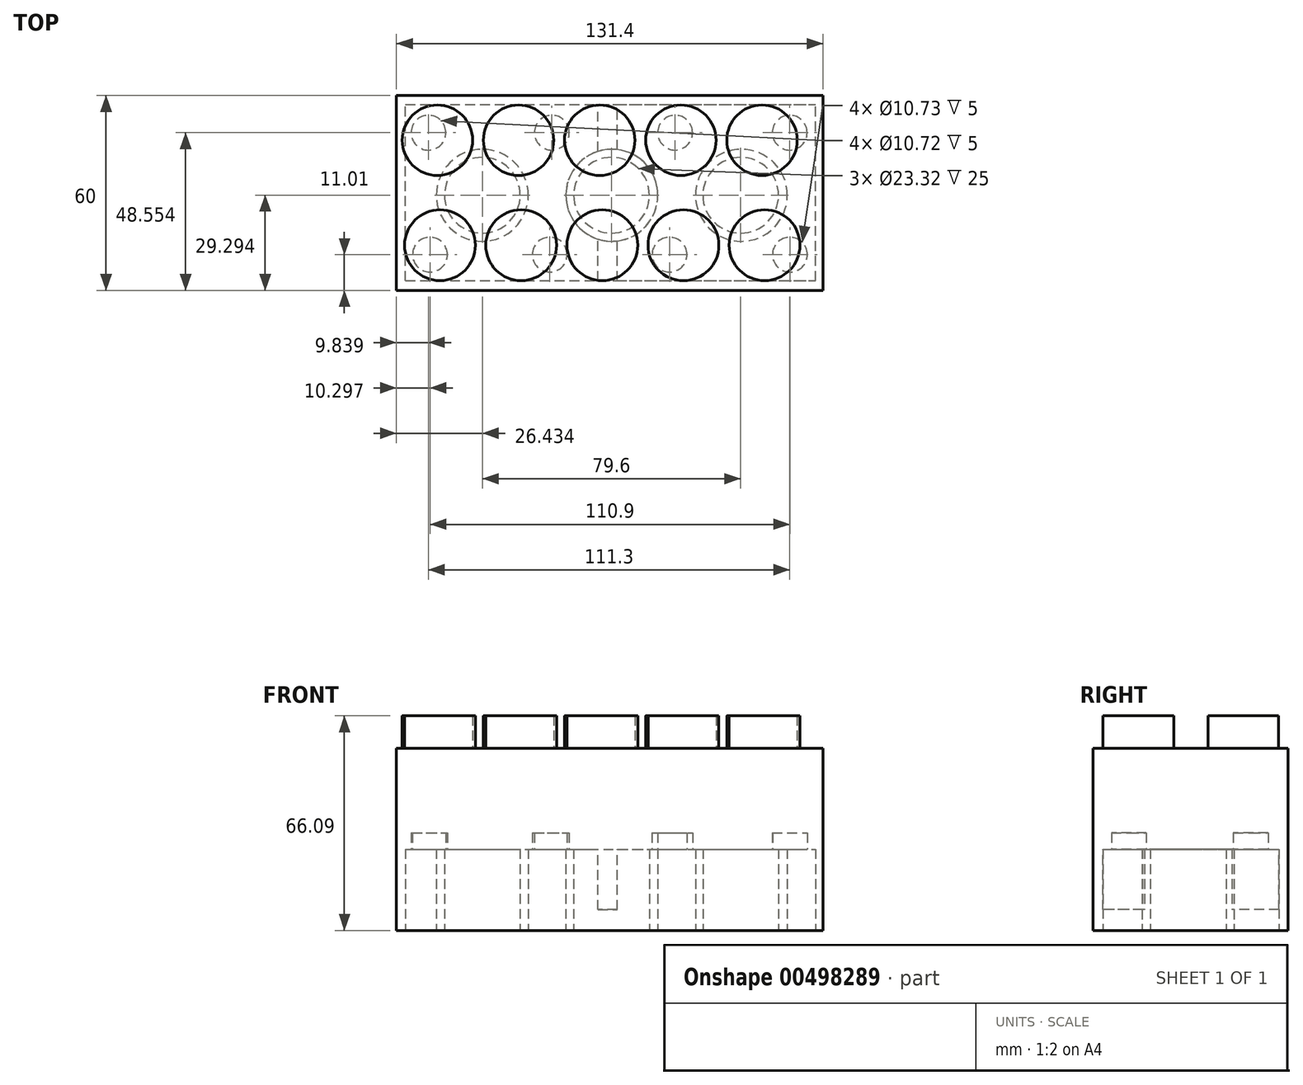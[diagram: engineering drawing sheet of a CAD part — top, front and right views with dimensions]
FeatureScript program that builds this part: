
annotation { "Feature Type Name" : "Feature", "Feature Type Description" : "" }
export const myFeature = defineFeature(function(context is Context, id is Id, definition is map)
    precondition{}
    {
        {
            var Q0;
            Q0=qCreatedBy(makeId("Front.planeOp"),FACE);
            var sketch = newSketch(context, id + "F0", { "sketchPlane" : qUnion([Q0])});
            skLineSegment(sketch, "E0.bottom", {"start": v(-65.01, 21.75) * mm, "end": v(66.39, 21.75) * mm});
            skLineSegment(sketch, "E0.top", {"start": v(-65.01, -34.34) * mm, "end": v(66.39, -34.34) * mm});
            skLineSegment(sketch, "E0.left", {"start": v(-65.01, 21.75) * mm, "end": v(-65.01, -34.34) * mm});
            skLineSegment(sketch, "E0.right", {"start": v(66.39, 21.75) * mm, "end": v(66.39, -34.34) * mm});
            skSolve(sketch);
        }
        {
            var Q0;
            Q0=makeQuery(id+"F0.imprint","IMPRINT",FACE,{"disambiguationData":[TD([[makeQuery(id+"F0.imprint","IMPRINT",EDGE,{"derivedFrom":sQuery(id+"F0.wireOp",EDGE,"E0.bottom")}),-1.0]])]});
            extrude(context, id + "F1", {"entities" : qUnion([Q0]), "depth" : 60 * mm});
        }
        {
            var Q0;
            Q0=makeQuery(id+"F1.opExtrude","SWEPT_FACE",FACE,{"disambiguationData":[OSD([sQuery(id+"F0.wireOp",EDGE,"E0.bottom")])]});
            var sketch = newSketch(context, id + "F2", { "sketchPlane" : qUnion([Q0])});
            skCircle(sketch, "E1", {"center": v(-51.62, -46.09) * mm, "radius": 10.9 * mm});
            skCircle(sketch, "E2.1.0.0", {"center": v(-26.62, -46.09) * mm, "radius": 10.9 * mm});
            skCircle(sketch, "E2.2.0.0", {"center": v(-1.62, -46.09) * mm, "radius": 10.9 * mm});
            skLineSegment(sketch, "E2.direction1", {"start": v(-51.62, -46.09) * mm, "end": v(-26.62, -46.09) * mm, "construction": true});
            skCircle(sketch, "E3.1.0.0", {"center": v(23.38, -46.09) * mm, "radius": 10.9 * mm});
            skCircle(sketch, "E3.2.0.0", {"center": v(48.38, -46.09) * mm, "radius": 10.9 * mm});
            skLineSegment(sketch, "E3.direction1", {"start": v(-1.62, -46.09) * mm, "end": v(23.38, -46.09) * mm, "construction": true});
            skSolve(sketch);
        }
        {
            var Q0;
            Q0 = qSketchRegion(id + "F2", true);
            extrude(context, id + "F3", {"entities" : qUnion([Q0]), "operationType" : NewBodyOperationType.ADD, "depth" : 10 * mm});
        }
        {
            var Q0;
            Q0=makeQuery(id+"F1.opExtrude","SWEPT_FACE",FACE,{"disambiguationData":[OSD([sQuery(id+"F0.wireOp",EDGE,"E0.bottom")])]});
            var sketch = newSketch(context, id + "F4", { "sketchPlane" : qUnion([Q0])});
            skCircle(sketch, "E4", {"center": v(-52.41, -13.75) * mm, "radius": 10.84 * mm});
            skCircle(sketch, "E5.1.0.0", {"center": v(-27.41, -13.75) * mm, "radius": 10.84 * mm});
            skCircle(sketch, "E5.2.0.0", {"center": v(-2.41, -13.75) * mm, "radius": 10.84 * mm});
            skLineSegment(sketch, "E5.direction1", {"start": v(-52.41, -13.75) * mm, "end": v(-27.41, -13.75) * mm, "construction": true});
            skCircle(sketch, "E6.1.0.0", {"center": v(22.59, -13.75) * mm, "radius": 10.84 * mm});
            skCircle(sketch, "E6.2.0.0", {"center": v(47.59, -13.75) * mm, "radius": 10.84 * mm});
            skLineSegment(sketch, "E6.direction1", {"start": v(-2.41, -13.75) * mm, "end": v(22.59, -13.75) * mm, "construction": true});
            skSolve(sketch);
        }
        {
            var Q0;
            Q0=makeQuery(id+"F4.imprint","IMPRINT",FACE,{"disambiguationData":[TD([[makeQuery(id+"F4.imprint","IMPRINT",EDGE,{"derivedFrom":sQuery(id+"F4.wireOp",EDGE,"E4")}),1.0]])]});
            var Q1;
            Q1=makeQuery(id+"F4.imprint","IMPRINT",FACE,{"disambiguationData":[TD([[makeQuery(id+"F4.imprint","IMPRINT",EDGE,{"derivedFrom":sQuery(id+"F4.wireOp",EDGE,"E5.1.0.0")}),1.0]])]});
            var Q2;
            Q2=makeQuery(id+"F4.imprint","IMPRINT",FACE,{"disambiguationData":[TD([[makeQuery(id+"F4.imprint","IMPRINT",EDGE,{"derivedFrom":sQuery(id+"F4.wireOp",EDGE,"E5.2.0.0")}),1.0]])]});
            var Q3;
            Q3=makeQuery(id+"F4.imprint","IMPRINT",FACE,{"disambiguationData":[TD([[makeQuery(id+"F4.imprint","IMPRINT",EDGE,{"derivedFrom":sQuery(id+"F4.wireOp",EDGE,"E6.1.0.0")}),1.0]])]});
            var Q4;
            Q4=makeQuery(id+"F4.imprint","IMPRINT",FACE,{"disambiguationData":[TD([[makeQuery(id+"F4.imprint","IMPRINT",EDGE,{"derivedFrom":sQuery(id+"F4.wireOp",EDGE,"E6.2.0.0")}),1.0]])]});
            extrude(context, id + "F5", {"entities" : qUnion([Q0, Q1, Q2, Q3, Q4]), "operationType" : NewBodyOperationType.ADD, "depth" : 10 * mm});
        }
        {
            var Q0;
            Q0=makeQuery(id+"F1.opExtrude","SWEPT_FACE",FACE,{"disambiguationData":[OSD([sQuery(id+"F0.wireOp",EDGE,"E0.top")])]});
            var sketch = newSketch(context, id + "F6", { "sketchPlane" : qUnion([Q0])});
            skCircle(sketch, "E7", {"center": v(41.22, 30.7) * mm, "radius": 14.16 * mm});
            skCircle(sketch, "E8.1.0.0", {"center": v(1.32, 30.7) * mm, "radius": 14.16 * mm});
            skCircle(sketch, "E8.2.0.0", {"center": v(-38.58, 30.7) * mm, "radius": 14.16 * mm});
            skLineSegment(sketch, "E8.direction1", {"start": v(41.22, 30.7) * mm, "end": v(1.32, 30.7) * mm, "construction": true});
            skLineSegment(sketch, "E9.bottom", {"start": v(-62.27, 57) * mm, "end": v(64.1, 57) * mm});
            skLineSegment(sketch, "E9.top", {"start": v(-62.27, 2.75) * mm, "end": v(64.1, 2.75) * mm});
            skLineSegment(sketch, "E9.left", {"start": v(-62.27, 57) * mm, "end": v(-62.27, 2.75) * mm});
            skLineSegment(sketch, "E9.right", {"start": v(64.1, 57) * mm, "end": v(64.1, 2.75) * mm});
            skCircle(sketch, "E10", {"center": v(-38.58, 30.7) * mm, "radius": 11.66 * mm});
            skCircle(sketch, "E11.1.0.0", {"center": v(1.22, 30.7) * mm, "radius": 11.66 * mm});
            skCircle(sketch, "E11.2.0.0", {"center": v(41.02, 30.7) * mm, "radius": 11.66 * mm});
            skLineSegment(sketch, "E11.direction1", {"start": v(-38.58, 30.7) * mm, "end": v(1.22, 30.7) * mm, "construction": true});
            skCircle(sketch, "E12", {"center": v(-54.71, 48.99) * mm, "radius": 5.36 * mm});
            skCircle(sketch, "E13.1.0.0", {"center": v(-17.81, 48.99) * mm, "radius": 5.36 * mm});
            skCircle(sketch, "E13.2.0.0", {"center": v(19.09, 48.99) * mm, "radius": 5.36 * mm});
            skLineSegment(sketch, "E13.direction1", {"start": v(-54.71, 48.99) * mm, "end": v(-17.81, 48.99) * mm, "construction": true});
            skCircle(sketch, "E14.1.0.0", {"center": v(56.19, 48.99) * mm, "radius": 5.36 * mm});
            skCircle(sketch, "E14.2.0.0", {"center": v(93.29, 48.99) * mm, "radius": 5.36 * mm});
            skLineSegment(sketch, "E14.direction1", {"start": v(19.09, 48.99) * mm, "end": v(56.19, 48.99) * mm, "construction": true});
            skCircle(sketch, "E15", {"center": v(-55.17, 11.45) * mm, "radius": 5.36 * mm});
            skCircle(sketch, "E16.1.0.0", {"center": v(-17.17, 11.45) * mm, "radius": 5.36 * mm});
            skCircle(sketch, "E16.2.0.0", {"center": v(20.83, 11.45) * mm, "radius": 5.36 * mm});
            skLineSegment(sketch, "E16.direction1", {"start": v(-55.17, 11.45) * mm, "end": v(-17.17, 11.45) * mm, "construction": true});
            skCircle(sketch, "E17.1.0.0", {"center": v(56.13, 11.45) * mm, "radius": 5.36 * mm});
            skCircle(sketch, "E17.2.0.0", {"center": v(91.43, 11.45) * mm, "radius": 5.36 * mm});
            skLineSegment(sketch, "E17.direction1", {"start": v(20.83, 11.45) * mm, "end": v(56.13, 11.45) * mm, "construction": true});
            skSolve(sketch);
        }
        {
            var Q0;
            Q0=makeQuery(id+"F6.imprint","IMPRINT",FACE,{"disambiguationData":[TD([[makeQuery(id+"F6.imprint","IMPRINT",EDGE,{"derivedFrom":sQuery(id+"F6.wireOp",EDGE,"E7")}),-1.0]])]});
            var Q1;
            Q1=makeQuery(id+"F6.imprint","IMPRINT",FACE,{"disambiguationData":[TD([[makeQuery(id+"F6.imprint","IMPRINT",EDGE,{"derivedFrom":sQuery(id+"F6.wireOp",EDGE,"E10")}),1.0]])]});
            var Q2;
            Q2=makeQuery(id+"F6.imprint","IMPRINT",FACE,{"disambiguationData":[TD([[makeQuery(id+"F6.imprint","IMPRINT",EDGE,{"derivedFrom":sQuery(id+"F6.wireOp",EDGE,"E11.1.0.0")}),1.0]])]});
            var Q3;
            Q3=makeQuery(id+"F6.imprint","IMPRINT",FACE,{"disambiguationData":[TD([[makeQuery(id+"F6.imprint","IMPRINT",EDGE,{"derivedFrom":sQuery(id+"F6.wireOp",EDGE,"E11.2.0.0")}),1.0]])]});
            extrude(context, id + "F7", {"entities" : qUnion([Q0, Q1, Q2, Q3]), "operationType" : NewBodyOperationType.REMOVE, "oppositeDirection" : true, "depth" : 25 * mm});
        }
        {
            var Q0;
            Q0=makeQuery(id+"F7.boolean.opBoolean","SPLIT",FACE,{"disambiguationData":[TD([makeQuery(id+"F7.opExtrude","SWEPT_FACE",FACE,{"disambiguationData":[OSD([sQuery(id+"F6.wireOp",EDGE,"E12")])]})])],"derivedFrom":makeQuery(id+"F1.opExtrude","SWEPT_FACE",FACE,{"disambiguationData":[OSD([sQuery(id+"F0.wireOp",EDGE,"E0.top")])]})});
            var Q1;
            Q1=makeQuery(id+"F7.boolean.opBoolean","SPLIT",FACE,{"disambiguationData":[TD([makeQuery(id+"F7.opExtrude","SWEPT_FACE",FACE,{"disambiguationData":[OSD([sQuery(id+"F6.wireOp",EDGE,"E13.1.0.0")])]})])],"derivedFrom":makeQuery(id+"F1.opExtrude","SWEPT_FACE",FACE,{"disambiguationData":[OSD([sQuery(id+"F0.wireOp",EDGE,"E0.top")])]})});
            var Q2;
            Q2=makeQuery(id+"F7.boolean.opBoolean","SPLIT",FACE,{"disambiguationData":[TD([makeQuery(id+"F7.opExtrude","SWEPT_FACE",FACE,{"disambiguationData":[OSD([sQuery(id+"F6.wireOp",EDGE,"E13.2.0.0")])]})])],"derivedFrom":makeQuery(id+"F1.opExtrude","SWEPT_FACE",FACE,{"disambiguationData":[OSD([sQuery(id+"F0.wireOp",EDGE,"E0.top")])]})});
            var Q3;
            Q3=makeQuery(id+"F7.boolean.opBoolean","SPLIT",FACE,{"disambiguationData":[TD([makeQuery(id+"F7.opExtrude","SWEPT_FACE",FACE,{"disambiguationData":[OSD([sQuery(id+"F6.wireOp",EDGE,"E14.1.0.0")])]})])],"derivedFrom":makeQuery(id+"F1.opExtrude","SWEPT_FACE",FACE,{"disambiguationData":[OSD([sQuery(id+"F0.wireOp",EDGE,"E0.top")])]})});
            var Q4;
            Q4=makeQuery(id+"F7.boolean.opBoolean","SPLIT",FACE,{"disambiguationData":[TD([makeQuery(id+"F7.opExtrude","SWEPT_FACE",FACE,{"disambiguationData":[OSD([sQuery(id+"F6.wireOp",EDGE,"E17.1.0.0")])]})])],"derivedFrom":makeQuery(id+"F1.opExtrude","SWEPT_FACE",FACE,{"disambiguationData":[OSD([sQuery(id+"F0.wireOp",EDGE,"E0.top")])]})});
            var Q5;
            Q5=makeQuery(id+"F7.boolean.opBoolean","SPLIT",FACE,{"disambiguationData":[TD([makeQuery(id+"F7.opExtrude","SWEPT_FACE",FACE,{"disambiguationData":[OSD([sQuery(id+"F6.wireOp",EDGE,"E16.2.0.0")])]})])],"derivedFrom":makeQuery(id+"F1.opExtrude","SWEPT_FACE",FACE,{"disambiguationData":[OSD([sQuery(id+"F0.wireOp",EDGE,"E0.top")])]})});
            var Q6;
            Q6=makeQuery(id+"F7.boolean.opBoolean","SPLIT",FACE,{"disambiguationData":[TD([makeQuery(id+"F7.opExtrude","SWEPT_FACE",FACE,{"disambiguationData":[OSD([sQuery(id+"F6.wireOp",EDGE,"E16.1.0.0")])]})])],"derivedFrom":makeQuery(id+"F1.opExtrude","SWEPT_FACE",FACE,{"disambiguationData":[OSD([sQuery(id+"F0.wireOp",EDGE,"E0.top")])]})});
            var Q7;
            Q7=makeQuery(id+"F7.boolean.opBoolean","SPLIT",FACE,{"disambiguationData":[TD([makeQuery(id+"F7.opExtrude","SWEPT_FACE",FACE,{"disambiguationData":[OSD([sQuery(id+"F6.wireOp",EDGE,"E15")])]})])],"derivedFrom":makeQuery(id+"F1.opExtrude","SWEPT_FACE",FACE,{"disambiguationData":[OSD([sQuery(id+"F0.wireOp",EDGE,"E0.top")])]})});
            extrude(context, id + "F8", {"entities" : qUnion([Q0, Q1, Q2, Q3, Q4, Q5, Q6, Q7]), "operationType" : NewBodyOperationType.REMOVE, "oppositeDirection" : true, "depth" : 30 * mm});
        }
        {
            var Q0;
            Q0=makeQuery(id+"F1.opExtrude","SWEPT_FACE",FACE,{"disambiguationData":[OSD([sQuery(id+"F0.wireOp",EDGE,"E0.bottom")])]});
            var sketch = newSketch(context, id + "F9", { "sketchPlane" : qUnion([Q0])});
            skLineSegment(sketch, "E18.bottom", {"start": v(2.98, 0) * mm, "end": v(-2.98, 0) * mm});
            skLineSegment(sketch, "E18.top", {"start": v(2.98, -60) * mm, "end": v(-2.98, -60) * mm});
            skLineSegment(sketch, "E18.left", {"start": v(2.98, 0) * mm, "end": v(2.98, -60) * mm});
            skLineSegment(sketch, "E18.right", {"start": v(-2.98, 0) * mm, "end": v(-2.98, -60) * mm});
            skPoint(sketch, "E18.middle", {"position": v(0, -30) * mm});
            skPoint(sketch, "E18.middle.positionSnap0", {"position": v(66.39, -30) * mm});
            skPoint(sketch, "E18.centerSnap0", {"position": v(66.39, -30) * mm});
            skSolve(sketch);
        }
        {
            var Q0;
            Q0 = qSketchRegion(id + "F9", true);
            extrude(context, id + "F10", {"entities" : qUnion([Q0]), "operationType" : NewBodyOperationType.ADD, "oppositeDirection" : true, "depth" : 49.7 * mm});
        }
        {
            var Q0;
            Q0=makeQuery(id+"F7.boolean.opBoolean","SPLIT",FACE,{"disambiguationData":[TD([makeQuery(id+"F7.opExtrude","SWEPT_FACE",FACE,{"disambiguationData":[OSD([sQuery(id+"F6.wireOp",EDGE,"E8.1.0.0")])]})])],"derivedFrom":makeQuery(id+"F1.opExtrude","SWEPT_FACE",FACE,{"disambiguationData":[OSD([sQuery(id+"F0.wireOp",EDGE,"E0.top")])]})});
            var sketch = newSketch(context, id + "F11", { "sketchPlane" : qUnion([Q0])});
            skCircle(sketch, "E19.0", {"center": v(1.22, 30.7) * mm, "radius": 11.66 * mm});
            skSolve(sketch);
        }
        {
            var Q0;
            Q0 = qSketchRegion(id + "F11", true);
            var Q1;
            Q1=makeQuery(id+"F7.boolean.opBoolean","COPY",FACE,{"derivedFrom":makeQuery(id+"F7.opExtrude","CAP_FACE",FACE,{"disambiguationData":[OSD([sQuery(id+"F6.wireOp",EDGE,"E10")])],"isStart":false})});
            extrude(context, id + "F12", {"entities" : qUnion([Q0]), "operationType" : NewBodyOperationType.REMOVE, "endBound" : BoundingType.UP_TO_SURFACE, "oppositeDirection" : true, "endBoundEntityFace" : qUnion([Q1]), "depth" : 25 * mm});
        }
    });
